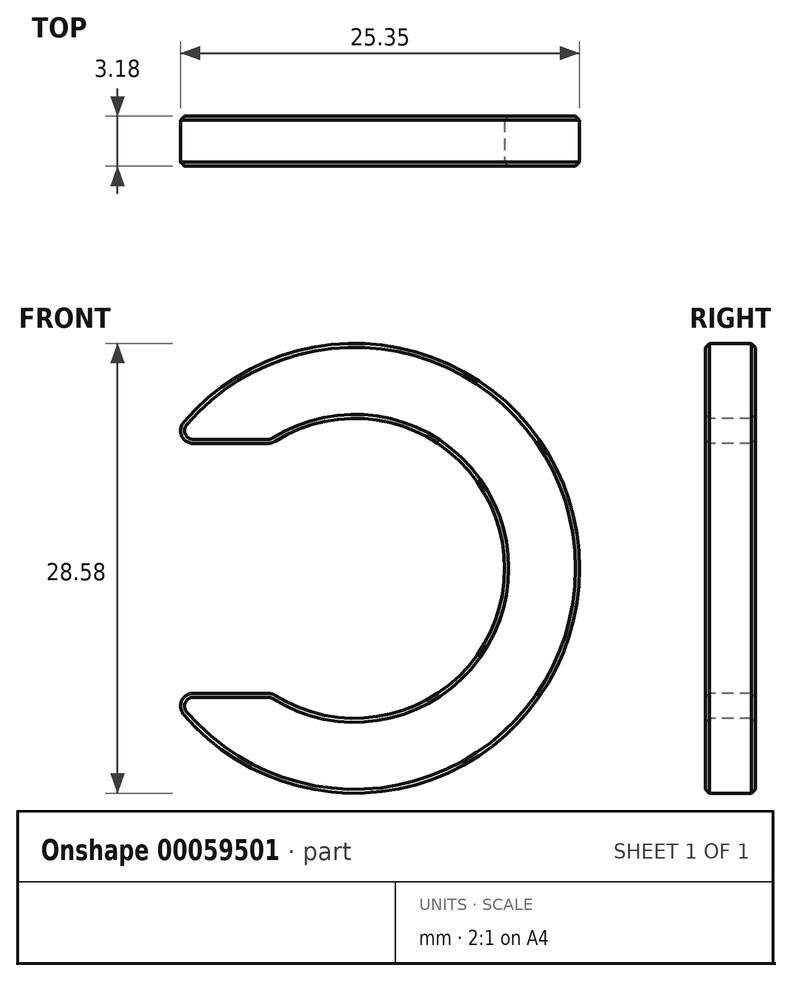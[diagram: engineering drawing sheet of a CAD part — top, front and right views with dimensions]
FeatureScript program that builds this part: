
annotation { "Feature Type Name" : "Feature", "Feature Type Description" : "" }
export const myFeature = defineFeature(function(context is Context, id is Id, definition is map)
    precondition{}
    {
        {
            var Q0;
            Q0=qCreatedBy(makeId("Front.planeOp"),FACE);
            var sketch = newSketch(context, id + "F0", { "sketchPlane" : qUnion([Q0])});
            skCircle(sketch, "E0", {"center": v(0, 0) * mm, "radius": 12.7 * mm, "construction": true});
            skArc(sketch, "E1", {"start": v(-10.87, -9.28) * mm, "mid": v(14.29, 0) * mm, "end": v(-10.87, 9.28) * mm});
            skArc(sketch, "E2", {"start": v(-5.07, -8.06) * mm, "mid": v(9.53, 0) * mm, "end": v(-5.07, 8.06) * mm});
            skLineSegment(sketch, "E3", {"start": v(-10.25, 7.94) * mm, "end": v(-5.5, 7.94) * mm});
            skLineSegment(sketch, "E4", {"start": v(-10.25, -7.94) * mm, "end": v(-5.5, -7.94) * mm});
            skPoint(sketch, "E5.visualSharp", {"position": v(-11.88, 7.94) * mm});
            skArc(sketch, "E5.filletArc", {"start": v(-10.87, 9.28) * mm, "mid": v(-10.99, 8.4) * mm, "end": v(-10.25, 7.94) * mm});
            skPoint(sketch, "E6.visualSharp", {"position": v(-5.27, 7.94) * mm});
            skArc(sketch, "E6.filletArc", {"start": v(-5.5, 7.94) * mm, "mid": v(-5.28, 7.97) * mm, "end": v(-5.07, 8.06) * mm});
            skPoint(sketch, "E7.visualSharp", {"position": v(-11.88, -7.94) * mm});
            skArc(sketch, "E7.filletArc", {"start": v(-10.25, -7.94) * mm, "mid": v(-10.99, -8.4) * mm, "end": v(-10.87, -9.28) * mm});
            skPoint(sketch, "E8.visualSharp", {"position": v(-5.27, -7.94) * mm});
            skArc(sketch, "E8.filletArc", {"start": v(-5.07, -8.06) * mm, "mid": v(-5.28, -7.97) * mm, "end": v(-5.5, -7.94) * mm});
            skSolve(sketch);
        }
        {
            var Q0;
            Q0 = qSketchRegion(id + "F0", true);
            extrude(context, id + "F1", {"entities" : qUnion([Q0]), "oppositeDirection" : true, "depth" : 3.17 * mm});
        }
        {
            var Q0;
            Q0=makeQuery(id+"F1.opExtrude","CAP_EDGE",EDGE,{"disambiguationData":[OSD([sQuery(id+"F0.wireOp",EDGE,"E2")])],"isStart":true});
            var Q1;
            Q1=makeQuery(id+"F1.opExtrude","CAP_EDGE",EDGE,{"disambiguationData":[OSD([sQuery(id+"F0.wireOp",EDGE,"E2")])],"isStart":false});
            chamfer(context, id + "F2", {"entities" : qUnion([Q0, Q1]), "width" : 0.25 * mm, "tangentPropagation" : true});
        }
    });
